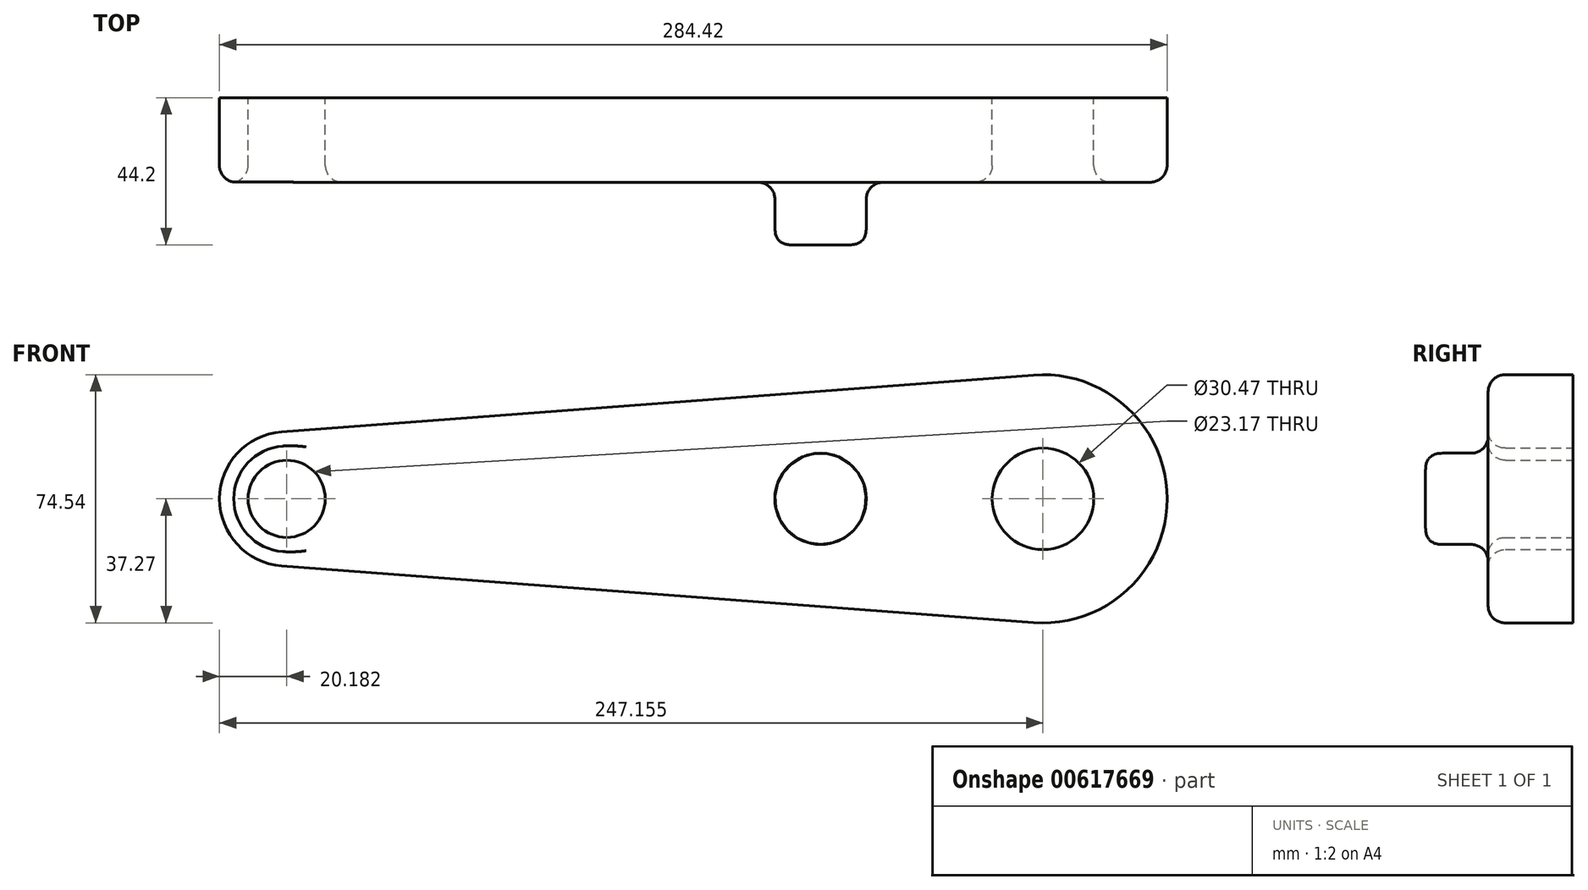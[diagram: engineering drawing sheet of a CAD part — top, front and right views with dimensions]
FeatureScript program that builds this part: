
annotation { "Feature Type Name" : "Feature", "Feature Type Description" : "" }
export const myFeature = defineFeature(function(context is Context, id is Id, definition is map)
    precondition{}
    {
        {
            var Q0;
            Q0=qCreatedBy(makeId("Front.planeOp"),FACE);
            var sketch = newSketch(context, id + "F0", { "sketchPlane" : qUnion([Q0])});
            skCircle(sketch, "E0", {"center": v(109.66, 0) * mm, "radius": 37.27 * mm});
            skCircle(sketch, "E1", {"center": v(-117.3, 0) * mm, "radius": 20.18 * mm});
            skLineSegment(sketch, "E2", {"start": v(-118.83, 20.13) * mm, "end": v(106.86, 37.16) * mm});
            skLineSegment(sketch, "E3", {"start": v(106.86, -37.16) * mm, "end": v(-118.83, -20.13) * mm});
            skCircle(sketch, "E4", {"center": v(109.66, 0) * mm, "radius": 15.24 * mm});
            skCircle(sketch, "E5", {"center": v(-117.3, 0) * mm, "radius": 11.58 * mm});
            skSolve(sketch);
        }
        {
            var Q0;
            Q0 = qSketchRegion(id + "F0", true);
            extrude(context, id + "F1", {"entities" : qUnion([Q0]), "depth" : 25.4 * mm, "offsetDistance" : 25.4 * mm});
        }
        {
            var Q0;
            Q0=makeQuery(id+"F1.opExtrude","CAP_FACE",FACE,{"disambiguationData":[OSD([sQuery(id+"F0.wireOp",EDGE,"E0"),sQuery(id+"F0.wireOp",EDGE,"E1"),sQuery(id+"F0.wireOp",EDGE,"E2"),sQuery(id+"F0.wireOp",EDGE,"E3"),sQuery(id+"F0.wireOp",EDGE,"E4"),sQuery(id+"F0.wireOp",EDGE,"E5")])],"isStart":false});
            fillet(context, id + "F2", {"entities" : qUnion([Q0]), "radius" : 5.08 * mm, "tangentPropagation" : true, "allowEdgeOverflow" : false});
        }
        {
            var Q0;
            Q0=qCreatedBy(makeId("Front.planeOp"),FACE);
            var sketch = newSketch(context, id + "F3", { "sketchPlane" : qUnion([Q0])});
            skCircle(sketch, "E6", {"center": v(42.92, 0) * mm, "radius": 13.7 * mm});
            skSolve(sketch);
        }
        {
            var Q0;
            Q0 = qSketchRegion(id + "F3", true);
            var Q1;
            Q1=makeQuery(id+"F1.opExtrude","CAP_FACE",FACE,{"disambiguationData":[OSD([sQuery(id+"F0.wireOp",EDGE,"E0"),sQuery(id+"F0.wireOp",EDGE,"E1"),sQuery(id+"F0.wireOp",EDGE,"E2"),sQuery(id+"F0.wireOp",EDGE,"E3"),sQuery(id+"F0.wireOp",EDGE,"E4"),sQuery(id+"F0.wireOp",EDGE,"E5")])],"isStart":false});
            extrude(context, id + "F4", {"entities" : qUnion([Q0]), "operationType" : NewBodyOperationType.ADD, "depth" : 44.2 * mm, "endBoundEntityFace" : qUnion([Q1]), "offsetDistance" : 25.4 * mm});
        }
        {
            var Q0;
            Q0=makeQuery(id+"F4.opExtrude","CAP_EDGE",EDGE,{"disambiguationData":[OSD([sQuery(id+"F3.wireOp",EDGE,"E6")])],"isStart":false});
            fillet(context, id + "F5", {"entities" : qUnion([Q0]), "radius" : 5.08 * mm, "tangentPropagation" : true, "rho" : 0.5, "crossSection" : FilletCrossSection.CONIC, "allowEdgeOverflow" : false});
        }
        {
            var Q0;
            Q0=makeQuery(id+"F4.boolean.opBoolean","INTERSECT",EDGE,{"derivedFrom":[makeQuery(id+"F1.opExtrude","CAP_FACE",FACE,{"disambiguationData":[OSD([sQuery(id+"F0.wireOp",EDGE,"E0"),sQuery(id+"F0.wireOp",EDGE,"E1"),sQuery(id+"F0.wireOp",EDGE,"E2"),sQuery(id+"F0.wireOp",EDGE,"E3"),sQuery(id+"F0.wireOp",EDGE,"E4"),sQuery(id+"F0.wireOp",EDGE,"E5")])],"isStart":false}),makeQuery(id+"F4.opExtrude","SWEPT_FACE",FACE,{"disambiguationData":[OSD([sQuery(id+"F3.wireOp",EDGE,"E6")])]})]});
            fillet(context, id + "F6", {"entities" : qUnion([Q0]), "radius" : 5.08 * mm, "tangentPropagation" : true, "allowEdgeOverflow" : false});
        }
    });
